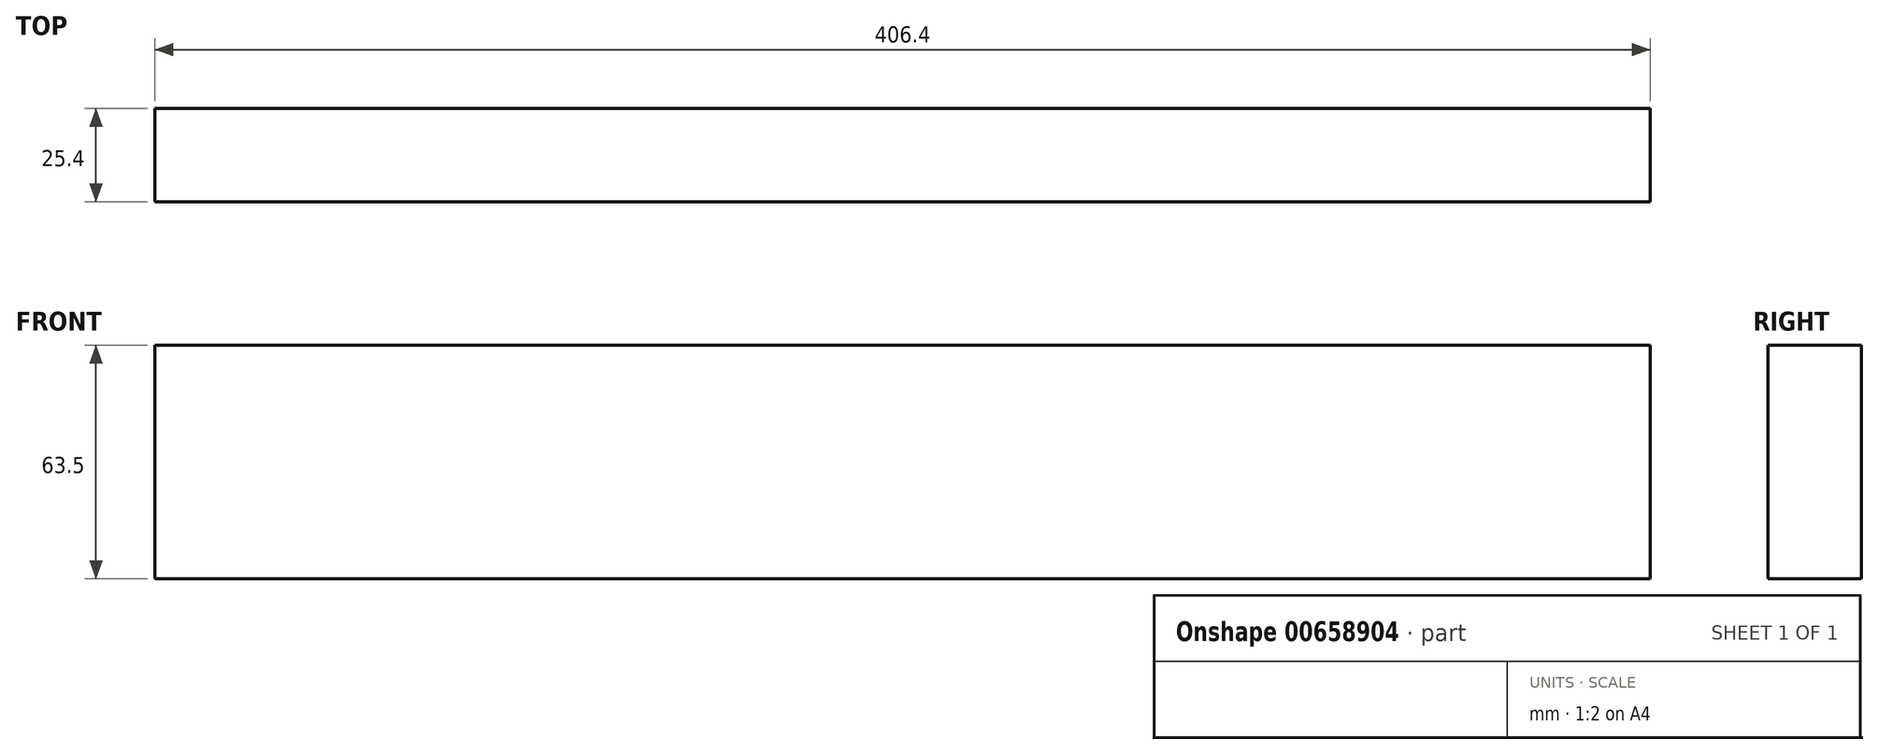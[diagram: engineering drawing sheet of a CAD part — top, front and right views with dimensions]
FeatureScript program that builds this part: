
annotation { "Feature Type Name" : "Feature", "Feature Type Description" : "" }
export const myFeature = defineFeature(function(context is Context, id is Id, definition is map)
    precondition{}
    {
        {
            var Q0;
            Q0=qCreatedBy(makeId("Front.planeOp"),FACE);
            var sketch = newSketch(context, id + "F0", { "sketchPlane" : qUnion([Q0])});
            skLineSegment(sketch, "E0.bottom", {"start": v(203.2, 31.75) * mm, "end": v(-203.2, 31.75) * mm});
            skLineSegment(sketch, "E0.top", {"start": v(203.2, -31.75) * mm, "end": v(-203.2, -31.75) * mm});
            skLineSegment(sketch, "E0.left", {"start": v(203.2, 31.75) * mm, "end": v(203.2, -31.75) * mm});
            skLineSegment(sketch, "E0.right", {"start": v(-203.2, 31.75) * mm, "end": v(-203.2, -31.75) * mm});
            skPoint(sketch, "E0.middle", {"position": v(0, 0) * mm});
            skSolve(sketch);
        }
        {
            var Q0;
            Q0=makeQuery(id+"F0.imprint","IMPRINT",FACE,{"disambiguationData":[TD([[makeQuery(id+"F0.imprint","IMPRINT",EDGE,{"derivedFrom":sQuery(id+"F0.wireOp",EDGE,"E0.bottom")}),1.0]])]});
            extrude(context, id + "F1", {"entities" : qUnion([Q0]), "depth" : 25.4 * mm, "offsetDistance" : 25.4 * mm});
        }
    });
